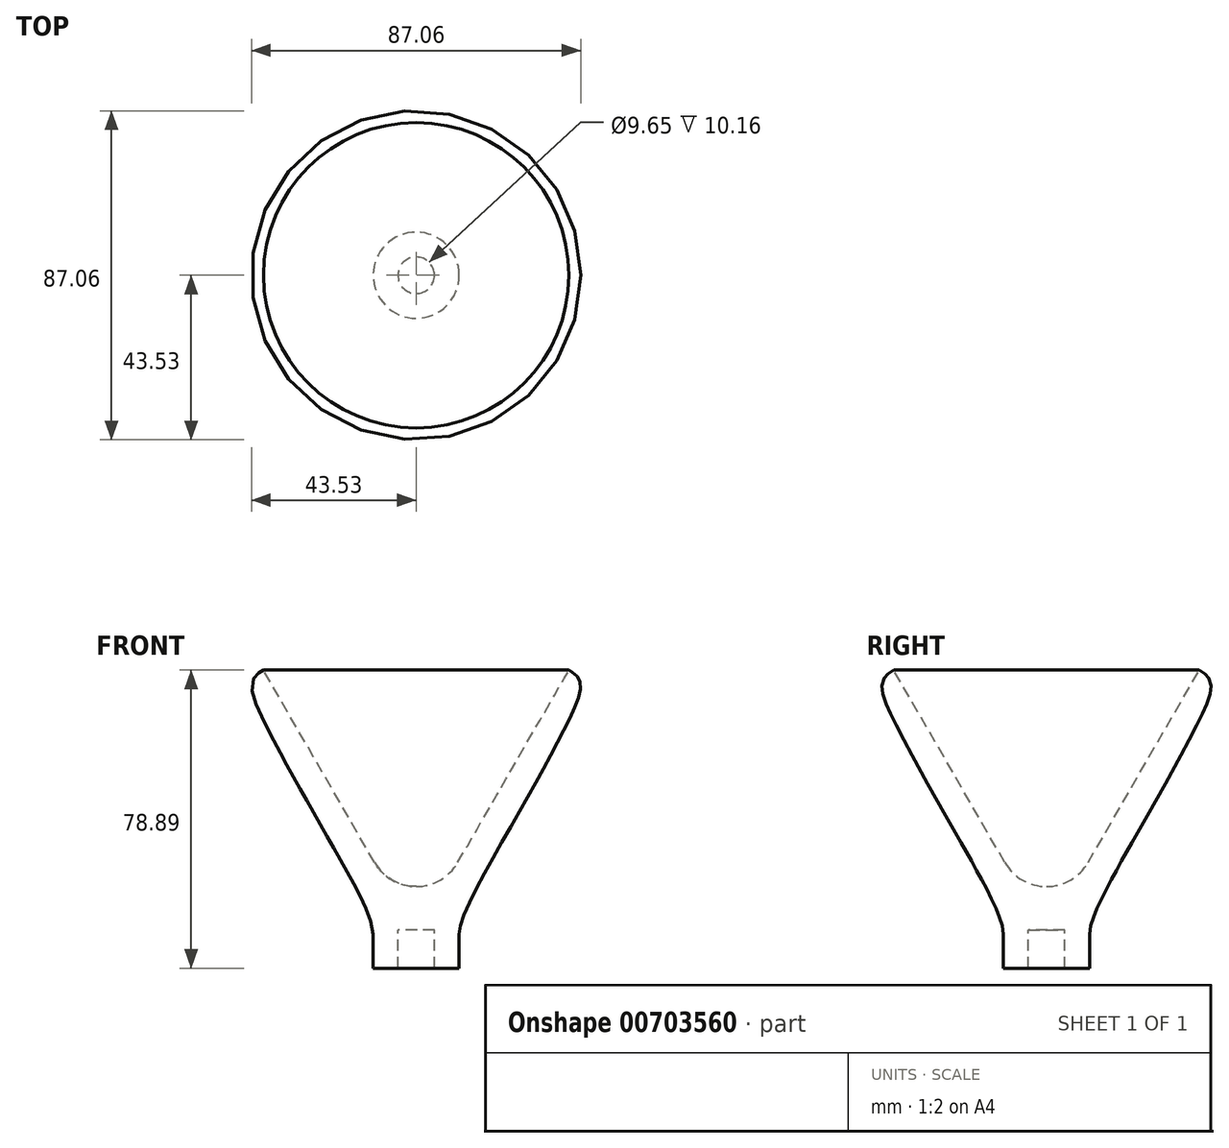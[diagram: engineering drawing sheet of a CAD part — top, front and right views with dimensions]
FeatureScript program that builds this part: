
annotation { "Feature Type Name" : "Feature", "Feature Type Description" : "" }
export const myFeature = defineFeature(function(context is Context, id is Id, definition is map)
    precondition{}
    {
        {
            var Q0;
            Q0=qCreatedBy(makeId("Front.planeOp"),FACE);
            var sketch = newSketch(context, id + "F0", { "sketchPlane" : qUnion([Q0])});
            skLineSegment(sketch, "E0", {"start": v(4.83, -13.65) * mm, "end": v(4.83, -3.5) * mm});
            skLineSegment(sketch, "E1", {"start": v(4.83, -3.5) * mm, "end": v(0, -3.5) * mm});
            skLineSegment(sketch, "E2", {"start": v(40.4, 65.24) * mm, "end": v(11, 14.3) * mm});
            skLineSegment(sketch, "E3", {"start": v(4.83, -13.65) * mm, "end": v(11.39, -13.65) * mm});
            skLineSegment(sketch, "E4", {"start": v(11.39, -13.65) * mm, "end": v(11.39, -4.74) * mm});
            skLineSegment(sketch, "E5", {"start": v(40.86, 64.98) * mm, "end": v(40.4, 65.24) * mm, "construction": true});
            skArc(sketch, "E6", {"start": v(0, 7.96) * mm, "mid": v(6.35, 9.66) * mm, "end": v(11, 14.3) * mm});
            skLineSegment(sketch, "E7", {"start": v(0, 7.96) * mm, "end": v(-6.94, 7.96) * mm, "construction": true});
            skFitSpline(sketch, "E8", {"points": [v(40.4, 65.24) * mm, v(43.17, 62.75) * mm, v(39.78, 50.75) * mm, v(23.77, 21.54) * mm, v(11.39, -4.74) * mm], "startDerivative": vector(11.6, -6.7) * mm, "endDerivative": vector(0, -45.81) * mm});
            skPoint(sketch, "E9.orphan", {"position": v(0, -4.74) * mm});
            skLineSegment(sketch, "E10", {"start": v(0, 7.96) * mm, "end": v(0, -3.5) * mm});
            skCircle(sketch, "E11", {"center": v(0, 43.56) * mm, "radius": 19.05 * mm});
            skLineSegment(sketch, "E12", {"start": v(40.4, 65.24) * mm, "end": v(40.4, 65.24) * mm});
            skSolve(sketch);
        }
        {
            var Q0;
            Q0=makeQuery(id+"F0.imprint","IMPRINT",FACE,{"disambiguationData":[TD([[makeQuery(id+"F0.imprint","IMPRINT",EDGE,{"derivedFrom":sQuery(id+"F0.wireOp",EDGE,"E0")}),-1.0]])]});
            var Q1;
            Q1=sQuery(id+"F0.wireOp",EDGE,"E10");
            revolve(context, id + "F1", {"surfaceOperationType" : NewSurfaceOperationType.NEW, "entities" : qUnion([Q0]), "axis" : qUnion([Q1]), "revolveType" : RevolveType.FULL});
        }
    });
